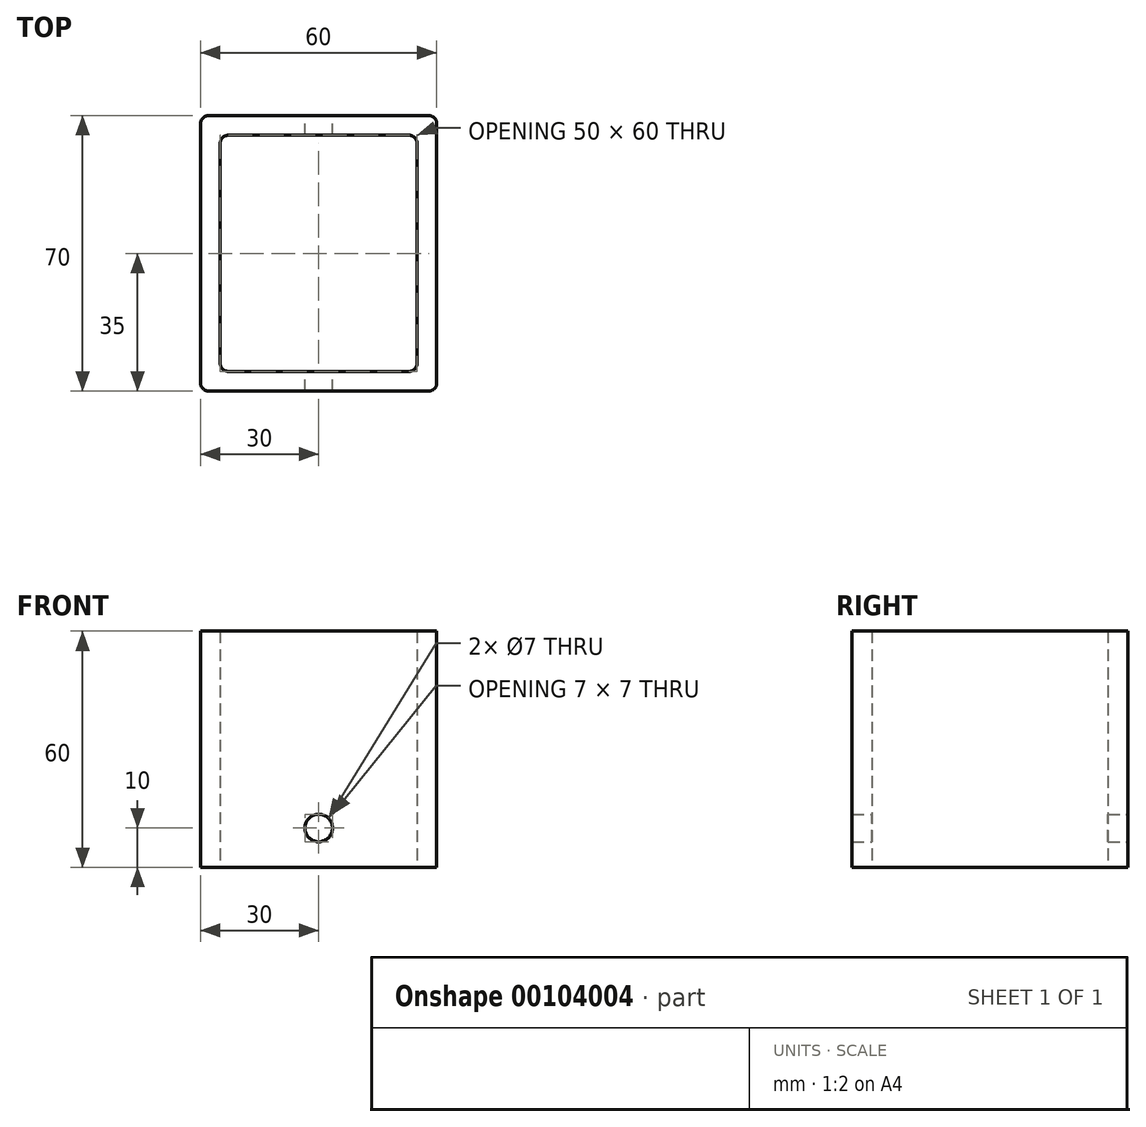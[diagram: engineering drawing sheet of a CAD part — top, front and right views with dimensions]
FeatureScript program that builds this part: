
annotation { "Feature Type Name" : "Feature", "Feature Type Description" : "" }
export const myFeature = defineFeature(function(context is Context, id is Id, definition is map)
    precondition{}
    {
        {
            var Q0;
            Q0=qCreatedBy(makeId("Top.planeOp"),FACE);
            var sketch = newSketch(context, id + "F0", { "sketchPlane" : qUnion([Q0])});
            skLineSegment(sketch, "E0.bottom", {"start": v(30, 35) * mm, "end": v(-30, 35) * mm});
            skLineSegment(sketch, "E0.top", {"start": v(30, -35) * mm, "end": v(-30, -35) * mm});
            skLineSegment(sketch, "E0.left", {"start": v(30, 35) * mm, "end": v(30, -35) * mm});
            skLineSegment(sketch, "E0.right", {"start": v(-30, 35) * mm, "end": v(-30, -35) * mm});
            skPoint(sketch, "E0.middle", {"position": v(0, 0) * mm});
            skLineSegment(sketch, "E1.bottom", {"start": v(25, 30) * mm, "end": v(-25, 30) * mm});
            skLineSegment(sketch, "E1.top", {"start": v(25, -30) * mm, "end": v(-25, -30) * mm});
            skLineSegment(sketch, "E1.left", {"start": v(25, 30) * mm, "end": v(25, -30) * mm});
            skLineSegment(sketch, "E1.right", {"start": v(-25, 30) * mm, "end": v(-25, -30) * mm});
            skSolve(sketch);
        }
        {
            var Q0;
            Q0=makeQuery(id+"F0.imprint","IMPRINT",FACE,{"disambiguationData":[TD([[makeQuery(id+"F0.imprint","IMPRINT",EDGE,{"derivedFrom":sQuery(id+"F0.wireOp",EDGE,"E0.bottom")}),1.0]])]});
            extrude(context, id + "F1", {"entities" : qUnion([Q0]), "depth" : 60 * mm});
        }
        {
            var Q0;
            Q0=makeQuery(id+"F1.opExtrude","SWEPT_EDGE",EDGE,{"disambiguationData":[OSD([sQuery(id+"F0.wireOp",EDGE,"E0.bottom"),sQuery(id+"F0.wireOp",EDGE,"E0.right")])]});
            var Q1;
            Q1=makeQuery(id+"F1.opExtrude","SWEPT_EDGE",EDGE,{"disambiguationData":[OSD([sQuery(id+"F0.wireOp",EDGE,"E0.bottom"),sQuery(id+"F0.wireOp",EDGE,"E0.left")])]});
            var Q2;
            Q2=makeQuery(id+"F1.opExtrude","SWEPT_EDGE",EDGE,{"disambiguationData":[OSD([sQuery(id+"F0.wireOp",EDGE,"E0.top"),sQuery(id+"F0.wireOp",EDGE,"E0.left")])]});
            var Q3;
            Q3=makeQuery(id+"F1.opExtrude","SWEPT_EDGE",EDGE,{"disambiguationData":[OSD([sQuery(id+"F0.wireOp",EDGE,"E0.top"),sQuery(id+"F0.wireOp",EDGE,"E0.right")])]});
            var Q4;
            Q4=makeQuery(id+"F1.opExtrude","SWEPT_EDGE",EDGE,{"disambiguationData":[OSD([sQuery(id+"F0.wireOp",EDGE,"E1.bottom"),sQuery(id+"F0.wireOp",EDGE,"E1.right")])]});
            var Q5;
            Q5=makeQuery(id+"F1.opExtrude","SWEPT_EDGE",EDGE,{"disambiguationData":[OSD([sQuery(id+"F0.wireOp",EDGE,"E1.bottom"),sQuery(id+"F0.wireOp",EDGE,"E1.left")])]});
            var Q6;
            Q6=makeQuery(id+"F1.opExtrude","SWEPT_EDGE",EDGE,{"disambiguationData":[OSD([sQuery(id+"F0.wireOp",EDGE,"E1.top"),sQuery(id+"F0.wireOp",EDGE,"E1.left")])]});
            var Q7;
            Q7=makeQuery(id+"F1.opExtrude","SWEPT_EDGE",EDGE,{"disambiguationData":[OSD([sQuery(id+"F0.wireOp",EDGE,"E1.top"),sQuery(id+"F0.wireOp",EDGE,"E1.right")])]});
            fillet(context, id + "F2", {"entities" : qUnion([Q0, Q1, Q2, Q3, Q4, Q5, Q6, Q7]), "radius" : 2 * mm, "tangentPropagation" : true, "allowEdgeOverflow" : false});
        }
        {
            var Q0;
            Q0=makeQuery(id+"F1.opExtrude","SWEPT_FACE",FACE,{"disambiguationData":[OSD([sQuery(id+"F0.wireOp",EDGE,"E0.bottom")])]});
            var sketch = newSketch(context, id + "F3", { "sketchPlane" : qUnion([Q0])});
            skCircle(sketch, "E2", {"center": v(0, 10) * mm, "radius": 3.5 * mm});
            skSolve(sketch);
        }
        {
            var Q0;
            Q0=makeQuery(id+"F3.imprint","IMPRINT",FACE,{"disambiguationData":[TD([[makeQuery(id+"F3.imprint","IMPRINT",EDGE,{"derivedFrom":sQuery(id+"F3.wireOp",EDGE,"E2")}),1.0]])]});
            extrude(context, id + "F4", {"entities" : qUnion([Q0]), "operationType" : NewBodyOperationType.REMOVE, "oppositeDirection" : true, "depth" : 70 * mm});
        }
    });
